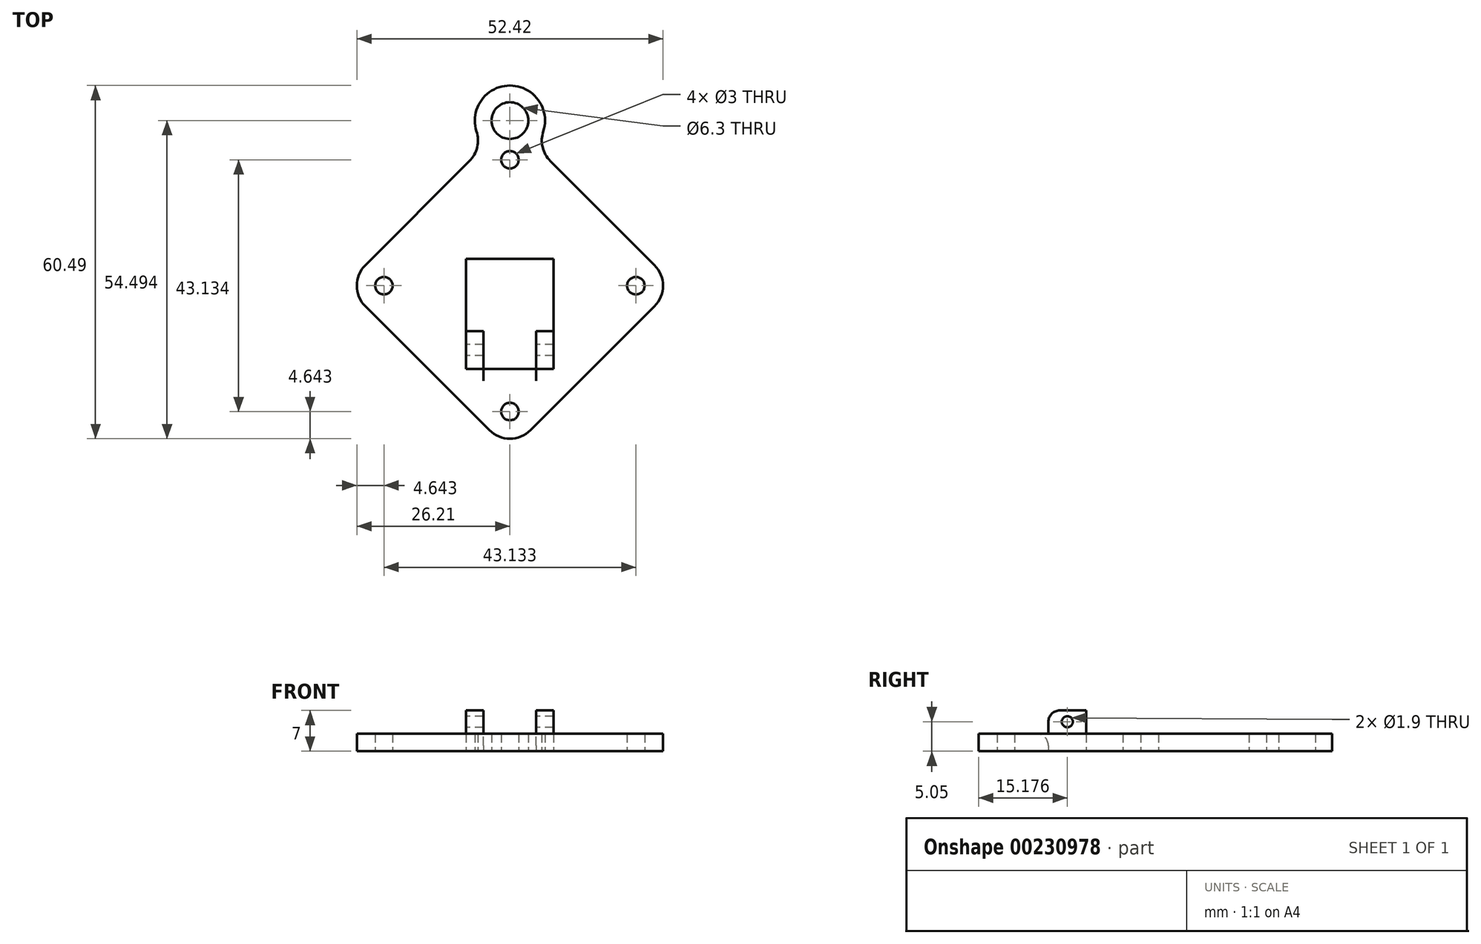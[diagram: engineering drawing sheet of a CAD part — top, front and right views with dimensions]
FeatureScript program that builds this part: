
annotation { "Feature Type Name" : "Feature", "Feature Type Description" : "" }
export const myFeature = defineFeature(function(context is Context, id is Id, definition is map)
    precondition{}
    {
        {
            var Q0;
            Q0=qCreatedBy(makeId("Top.planeOp"),FACE);
            var sketch = newSketch(context, id + "F0", { "sketchPlane" : qUnion([Q0])});
            skPoint(sketch, "E0.middle", {"position": v(0, 0) * mm});
            skLineSegment(sketch, "E1", {"start": v(-28.28, 0) * mm, "end": v(0, -28.28) * mm});
            skLineSegment(sketch, "E2", {"start": v(0, -28.28) * mm, "end": v(28.28, 0) * mm});
            skLineSegment(sketch, "E3", {"start": v(28.28, 0) * mm, "end": v(0, 28.28) * mm});
            skLineSegment(sketch, "E4", {"start": v(0, 28.28) * mm, "end": v(-28.28, 0) * mm});
            skLineSegment(sketch, "E5", {"start": v(-45.17, 0) * mm, "end": v(48.12, 0) * mm});
            skLineSegment(sketch, "E6", {"start": v(0, 40.83) * mm, "end": v(0, -39.1) * mm});
            skCircle(sketch, "E7", {"center": v(0, 21.57) * mm, "radius": 1.5 * mm});
            skCircle(sketch, "E8", {"center": v(21.57, 0) * mm, "radius": 1.5 * mm});
            skCircle(sketch, "E9", {"center": v(0, -21.57) * mm, "radius": 1.5 * mm});
            skCircle(sketch, "E10", {"center": v(-21.57, 0) * mm, "radius": 1.5 * mm});
            skCircle(sketch, "E11", {"center": v(0, 28.28) * mm, "radius": 6 * mm});
            skCircle(sketch, "E12", {"center": v(0, 28.28) * mm, "radius": 3.15 * mm});
            skLineSegment(sketch, "E13.bottom", {"start": v(-7.5, -7.78) * mm, "end": v(-4.5, -7.78) * mm});
            skLineSegment(sketch, "E13.top", {"start": v(-7.5, -14.28) * mm, "end": v(-4.5, -14.28) * mm});
            skLineSegment(sketch, "E13.left", {"start": v(-7.5, -7.78) * mm, "end": v(-7.5, -14.28) * mm});
            skLineSegment(sketch, "E13.right", {"start": v(-4.5, -7.78) * mm, "end": v(-4.5, -14.28) * mm});
            skLineSegment(sketch, "E14.MirrorCS", {"start": v(7.5, -7.78) * mm, "end": v(4.5, -7.78) * mm});
            skLineSegment(sketch, "E15.MirrorCS", {"start": v(4.5, -7.78) * mm, "end": v(4.5, -14.28) * mm});
            skLineSegment(sketch, "E16.MirrorCS", {"start": v(7.5, -7.78) * mm, "end": v(7.5, -14.28) * mm});
            skLineSegment(sketch, "E17.MirrorCS", {"start": v(7.5, -14.28) * mm, "end": v(4.5, -14.28) * mm});
            skLineSegment(sketch, "E18.bottom", {"start": v(-7.5, -7.78) * mm, "end": v(7.5, -7.78) * mm});
            skLineSegment(sketch, "E18.top", {"start": v(-7.5, 4.6) * mm, "end": v(7.5, 4.6) * mm});
            skLineSegment(sketch, "E18.left", {"start": v(-7.5, -7.78) * mm, "end": v(-7.5, 4.6) * mm});
            skLineSegment(sketch, "E18.right", {"start": v(7.5, -7.78) * mm, "end": v(7.5, 4.6) * mm});
            skLineSegment(sketch, "E19", {"start": v(-4.5, -14.28) * mm, "end": v(4.5, -14.28) * mm});
            skSolve(sketch);
        }
        {
            var Q0;
            Q0=makeQuery(id+"F0.imprint","IMPRINT",FACE,{"disambiguationData":[TD([[makeQuery(id+"F0.imprint","IMPRINT",EDGE,{"derivedFrom":sQuery(id+"F0.wireOp",EDGE,"E0.bottom")}),1.0]])]});
            var Q1;
            {var subQ7=sQuery(id+"F0.wireOp",EDGE,"E1");Q1=makeQuery(id+"F0.imprint","IMPRINT",FACE,{"disambiguationData":[TD([[makeQuery(id+"F0.imprint","IMPRINT",EDGE,{"derivedFrom":subQ7}),1.0]])]});}
            var Q2;
            {var subQ5=sQuery(id+"F0.wireOp",EDGE,"E2");Q2=makeQuery(id+"F0.imprint","IMPRINT",FACE,{"disambiguationData":[TD([[makeQuery(id+"F0.imprint","IMPRINT",EDGE,{"derivedFrom":subQ5}),1.0]])]});}
            var Q3;
            {var subQ0=sQuery(id+"F0.wireOp",EDGE,"E6");var subQ3=sQuery(id+"F0.wireOp",EDGE,"YBWlPE1A-UsR7-Rr52-xMMV-lg8XNYewxg8Y");var subQ5=makeQuery(id+"F0.imprint","INTERSECT",VERTEX,{"disambiguationData":[OD(0.0)],"derivedFrom":[subQ0,subQ3]});Q3=makeQuery(id+"F0.imprint","IMPRINT",FACE,{"disambiguationData":[TD([[makeQuery(id+"F0.imprint","IMPRINT",EDGE,{"disambiguationData":[TD([[subQ5,-1.0]])],"derivedFrom":subQ3}),1.0]])]});}
            var Q4;
            {var subQ0=sQuery(id+"F0.wireOp",EDGE,"E6");var subQ3=sQuery(id+"F0.wireOp",EDGE,"YBWlPE1A-UsR7-Rr52-xMMV-lg8XNYewxg8Y");var subQ5=makeQuery(id+"F0.imprint","INTERSECT",VERTEX,{"disambiguationData":[OD(0.0)],"derivedFrom":[subQ0,subQ3]});Q4=makeQuery(id+"F0.imprint","IMPRINT",FACE,{"disambiguationData":[TD([[makeQuery(id+"F0.imprint","IMPRINT",EDGE,{"disambiguationData":[TD([[subQ5,1.0]])],"derivedFrom":subQ3}),1.0]])]});}
            var Q5;
            {var subQ5=sQuery(id+"F0.wireOp",EDGE,"E10");var subQ6=sQuery(id+"F0.wireOp",EDGE,"E5");var subQ7=makeQuery(id+"F0.imprint","INTERSECT",VERTEX,{"disambiguationData":[OD(1.0)],"derivedFrom":[subQ6,subQ5]});Q5=makeQuery(id+"F0.imprint","IMPRINT",FACE,{"disambiguationData":[TD([[makeQuery(id+"F0.imprint","IMPRINT",EDGE,{"disambiguationData":[TD([[subQ7,-1.0]])],"derivedFrom":subQ6}),1.0]])]});}
            var Q6;
            {var subQ0=sQuery(id+"F0.wireOp",EDGE,"E11");var subQ1=sQuery(id+"F0.wireOp",EDGE,"E4");var subQ2=makeQuery(id+"F0.imprint","INTERSECT",VERTEX,{"derivedFrom":[subQ1,subQ0]});Q6=makeQuery(id+"F0.imprint","IMPRINT",FACE,{"disambiguationData":[TD([[makeQuery(id+"F0.imprint","IMPRINT",EDGE,{"disambiguationData":[TD([[subQ2,1.0]])],"derivedFrom":subQ1}),-1.0]])]});}
            var Q7;
            {var subQ0=sQuery(id+"F0.wireOp",EDGE,"E11");var subQ1=sQuery(id+"F0.wireOp",EDGE,"E4");var subQ2=makeQuery(id+"F0.imprint","INTERSECT",VERTEX,{"derivedFrom":[subQ1,subQ0]});Q7=makeQuery(id+"F0.imprint","IMPRINT",FACE,{"disambiguationData":[TD([[makeQuery(id+"F0.imprint","IMPRINT",EDGE,{"disambiguationData":[TD([[subQ2,1.0]])],"derivedFrom":subQ1}),1.0]])]});}
            var Q8;
            {var subQ0=sQuery(id+"F0.wireOp",EDGE,"E11");var subQ1=sQuery(id+"F0.wireOp",EDGE,"E3");var subQ2=makeQuery(id+"F0.imprint","INTERSECT",VERTEX,{"derivedFrom":[subQ1,subQ0]});Q8=makeQuery(id+"F0.imprint","IMPRINT",FACE,{"disambiguationData":[TD([[makeQuery(id+"F0.imprint","IMPRINT",EDGE,{"disambiguationData":[TD([[subQ2,-1.0]])],"derivedFrom":subQ1}),-1.0]])]});}
            var Q9;
            {var subQ0=sQuery(id+"F0.wireOp",EDGE,"E11");var subQ1=sQuery(id+"F0.wireOp",EDGE,"E3");var subQ2=makeQuery(id+"F0.imprint","INTERSECT",VERTEX,{"derivedFrom":[subQ1,subQ0]});Q9=makeQuery(id+"F0.imprint","IMPRINT",FACE,{"disambiguationData":[TD([[makeQuery(id+"F0.imprint","IMPRINT",EDGE,{"disambiguationData":[TD([[subQ2,-1.0]])],"derivedFrom":subQ1}),1.0]])]});}
            var Q10;
            {var subQ0=sQuery(id+"F0.wireOp",EDGE,"E5");var subQ5=sQuery(id+"F0.wireOp",EDGE,"E18.right");var subQ10=makeQuery(id+"F0.imprint","INTERSECT",VERTEX,{"derivedFrom":[subQ0,subQ5]});Q10=makeQuery(id+"F0.imprint","IMPRINT",FACE,{"disambiguationData":[TD([[makeQuery(id+"F0.imprint","IMPRINT",EDGE,{"disambiguationData":[TD([[subQ10,-1.0]])],"derivedFrom":subQ0}),1.0]])]});}
            extrude(context, id + "F1", {"entities" : qUnion([Q0, Q1, Q2, Q3, Q4, Q5, Q6, Q7, Q8, Q9, Q10]), "depth" : 3 * mm});
        }
        {
            var Q0;
            Q0=makeQuery(id+"F1.opExtrude","SWEPT_EDGE",EDGE,{"disambiguationData":[OSD([sQuery(id+"F0.wireOp",EDGE,"E3"),sQuery(id+"F0.wireOp",EDGE,"YBWlPE1A-UsR7-Rr52-xMMV-lg8XNYewxg8Y")])]});
            var Q1;
            Q1=makeQuery(id+"F1.opExtrude","SWEPT_EDGE",EDGE,{"disambiguationData":[OSD([sQuery(id+"F0.wireOp",EDGE,"E4"),sQuery(id+"F0.wireOp",EDGE,"YBWlPE1A-UsR7-Rr52-xMMV-lg8XNYewxg8Y")])]});
            var Q2;
            Q2=makeQuery(id+"F1.opExtrude","SWEPT_EDGE",EDGE,{"disambiguationData":[OSD([sQuery(id+"F0.wireOp",EDGE,"E1"),sQuery(id+"F0.wireOp",EDGE,"E4"),sQuery(id+"F0.wireOp",EDGE,"E5")])]});
            var Q3;
            Q3=makeQuery(id+"F1.opExtrude","SWEPT_EDGE",EDGE,{"disambiguationData":[OSD([sQuery(id+"F0.wireOp",EDGE,"E2"),sQuery(id+"F0.wireOp",EDGE,"E3"),sQuery(id+"F0.wireOp",EDGE,"E5")])]});
            var Q4;
            Q4=makeQuery(id+"F1.opExtrude","SWEPT_EDGE",EDGE,{"disambiguationData":[OSD([sQuery(id+"F0.wireOp",EDGE,"E1"),sQuery(id+"F0.wireOp",EDGE,"E2"),sQuery(id+"F0.wireOp",EDGE,"E6")])]});
            fillet(context, id + "F2", {"entities" : qUnion([Q0, Q1, Q2, Q3, Q4]), "radius" : 5 * mm, "tangentPropagation" : true, "allowEdgeOverflow" : false});
        }
        {
            var Q0;
            Q0=makeQuery(id+"F0.imprint","IMPRINT",FACE,{"disambiguationData":[TD([[makeQuery(id+"F0.imprint","IMPRINT",EDGE,{"derivedFrom":sQuery(id+"F0.wireOp",EDGE,"E13.top")}),1.0]])]});
            var Q1;
            {var subQ0=sQuery(id+"F0.wireOp",EDGE,"E15.MirrorCS");Q1=makeQuery(id+"F0.imprint","IMPRINT",FACE,{"disambiguationData":[TD([[makeQuery(id+"F0.imprint","IMPRINT",EDGE,{"derivedFrom":subQ0}),1.0]])]});}
            extrude(context, id + "F3", {"entities" : qUnion([Q0, Q1]), "operationType" : NewBodyOperationType.ADD, "depth" : 7 * mm});
        }
        {
            var Q0;
            Q0=makeQuery(id+"F3.opExtrude","SWEPT_FACE",FACE,{"disambiguationData":[OSD([sQuery(id+"F0.wireOp",EDGE,"E13.left")])]});
            var sketch = newSketch(context, id + "F4", { "sketchPlane" : qUnion([Q0])});
            skCircle(sketch, "E20", {"center": v(11.03, 5.05) * mm, "radius": 0.95 * mm});
            skSolve(sketch);
        }
        {
            var Q0;
            Q0 = qSketchRegion(id + "F4", true);
            extrude(context, id + "F5", {"entities" : qUnion([Q0]), "operationType" : NewBodyOperationType.REMOVE, "oppositeDirection" : true, "depth" : 25 * mm});
        }
        {
            var Q0;
            Q0=makeQuery(id+"F3.opExtrude","CAP_EDGE",EDGE,{"disambiguationData":[OSD([sQuery(id+"F0.wireOp",EDGE,"E13.top")])],"isStart":false});
            var Q1;
            {var subQ0=sQuery(id+"F0.wireOp",EDGE,"E19");var subQ1=sQuery(id+"F0.wireOp",EDGE,"E17.MirrorCS");var subQ2=sQuery(id+"F0.wireOp",EDGE,"E13.top");Q1=makeQuery(id+"F3.boolean.opBoolean","SPLIT",EDGE,{"disambiguationData":[topologyDisambiguationEdgeConnected([makeQuery(id+"F3.opExtrude","SWEPT_FACE",FACE,{"disambiguationData":[OSD([subQ2])]})])],"derivedFrom":makeQuery(id+"F1.opExtrude","CAP_EDGE",EDGE,{"disambiguationData":[OSD([subQ2,subQ1,subQ0])],"isStart":false})});}
            var Q2;
            {var subQ0=sQuery(id+"F0.wireOp",EDGE,"E18.bottom");Q2=makeQuery(id+"F3.opExtrude","CAP_EDGE",EDGE,{"disambiguationData":[OSD([subQ0]),TDD([makeQuery(id+"F0.imprint","IMPRINT",EDGE,{"disambiguationData":[TD([[makeQuery(id+"F0.imprint","INTERSECT",VERTEX,{"derivedFrom":[sQuery(id+"F0.wireOp",EDGE,"E13.right"),subQ0]}),1.0]])],"derivedFrom":subQ0})])],"isStart":false});}
            var Q3;
            {var subQ0=sQuery(id+"F0.wireOp",EDGE,"E18.bottom");Q3=makeQuery(id+"F3.opExtrude","CAP_EDGE",EDGE,{"disambiguationData":[OSD([subQ0]),TDD([makeQuery(id+"F0.imprint","IMPRINT",EDGE,{"disambiguationData":[TD([[makeQuery(id+"F0.imprint","INTERSECT",VERTEX,{"derivedFrom":[sQuery(id+"F0.wireOp",EDGE,"E13.right"),subQ0]}),1.0]])],"derivedFrom":subQ0})])],"isStart":true});}
            var Q4;
            {var subQ0=sQuery(id+"F0.wireOp",EDGE,"E18.bottom");Q4=makeQuery(id+"F3.opExtrude","CAP_EDGE",EDGE,{"disambiguationData":[OSD([subQ0]),TDD([makeQuery(id+"F0.imprint","IMPRINT",EDGE,{"disambiguationData":[TD([[makeQuery(id+"F0.imprint","INTERSECT",VERTEX,{"derivedFrom":[sQuery(id+"F0.wireOp",EDGE,"E15.MirrorCS"),subQ0]}),-1.0]])],"derivedFrom":subQ0})])],"isStart":true});}
            var Q5;
            {var subQ0=sQuery(id+"F0.wireOp",EDGE,"E19");var subQ1=sQuery(id+"F0.wireOp",EDGE,"E17.MirrorCS");var subQ2=sQuery(id+"F0.wireOp",EDGE,"E13.top");Q5=makeQuery(id+"F3.boolean.opBoolean","SPLIT",EDGE,{"disambiguationData":[topologyDisambiguationEdgeConnected([makeQuery(id+"F3.opExtrude","SWEPT_FACE",FACE,{"disambiguationData":[OSD([subQ1])]})])],"derivedFrom":makeQuery(id+"F1.opExtrude","CAP_EDGE",EDGE,{"disambiguationData":[OSD([subQ2,subQ1,subQ0])],"isStart":false})});}
            var Q6;
            Q6=makeQuery(id+"F3.opExtrude","CAP_EDGE",EDGE,{"disambiguationData":[OSD([sQuery(id+"F0.wireOp",EDGE,"E17.MirrorCS")])],"isStart":false});
            var Q7;
            {var subQ0=sQuery(id+"F0.wireOp",EDGE,"E18.bottom");Q7=makeQuery(id+"F3.opExtrude","CAP_EDGE",EDGE,{"disambiguationData":[OSD([subQ0]),TDD([makeQuery(id+"F0.imprint","IMPRINT",EDGE,{"disambiguationData":[TD([[makeQuery(id+"F0.imprint","INTERSECT",VERTEX,{"derivedFrom":[sQuery(id+"F0.wireOp",EDGE,"E15.MirrorCS"),subQ0]}),-1.0]])],"derivedFrom":subQ0})])],"isStart":false});}
            fillet(context, id + "F6", {"entities" : qUnion([Q0, Q1, Q2, Q3, Q4, Q5, Q6, Q7]), "radius" : 2 * mm, "tangentPropagation" : true, "allowEdgeOverflow" : false});
        }
    });
